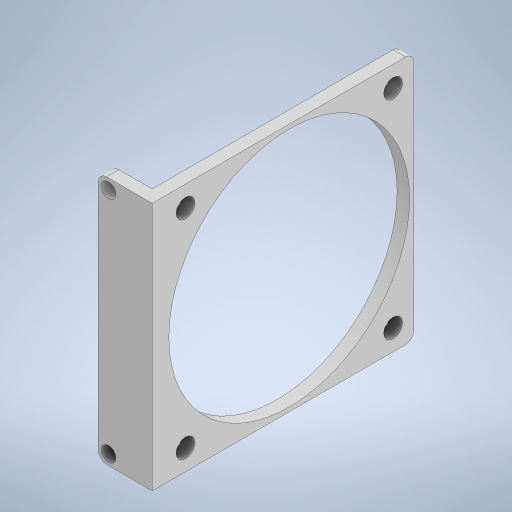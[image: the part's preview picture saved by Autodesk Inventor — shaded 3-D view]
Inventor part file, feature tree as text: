
AUTODESK INVENTOR PART (.ipt)
format: ipt  version: 2024 (Build 280153000, 153)  size: 286,720 bytes
history: native  units: mm
features: extrude x2, sketch x2, fillet x2
ambient origin geometry x8: Origin, YZ Plane, XZ Plane, XY Plane, X Axis, Y Axis, Z Axis, Center Point
bodies: Volumenkörper1 (feature_tree)
feature tree (6):
  extrude  "Extrusion1"  Depth=60.0mm
  sketch  "Skizze2"  dims[d3=5.0mm d4=5.0mm d5=5.0mm d6=5.0mm d7=4.5mm d8=4.5mm d9=4.5mm d10=4.5mm d11=3.0mm d12=0.0mm d13=13.0mm d14=1.5mm d17=2.5mm d18=2.5mm d19=2.5mm d21=3.5mm d23=3.5mm d28=2.0mm d29=3.0mm d30=0.0mm d31=2.0mm]
  fillet  "Rundung1"  Radius=58.0mm
  extrude  "Extrusion4"  Depth=2.0mm
  fillet  "Rundung2"  Radius=5.0mm
  sketch  "Skizze1"  dims[d0=60.0mm d1=60.0mm d2=58.0mm]
